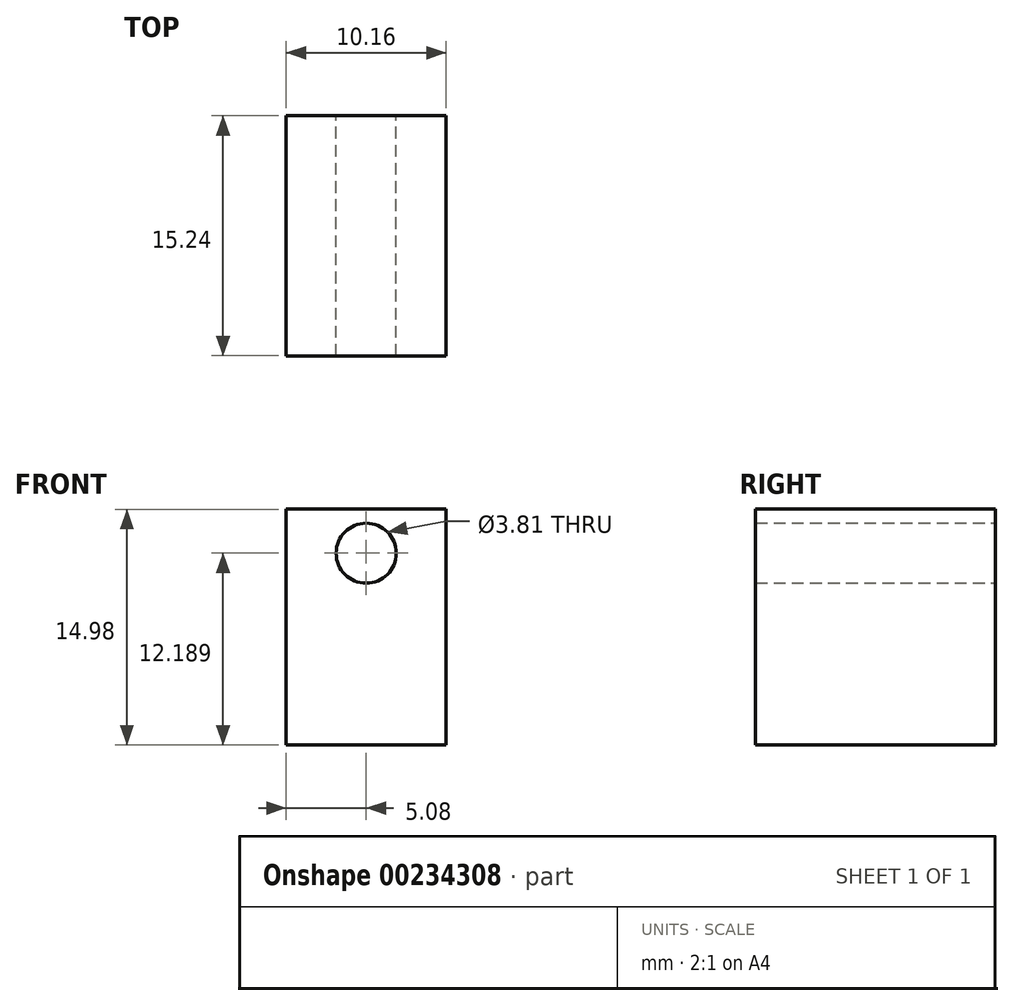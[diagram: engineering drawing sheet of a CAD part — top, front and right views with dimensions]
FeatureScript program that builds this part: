
annotation { "Feature Type Name" : "Feature", "Feature Type Description" : "" }
export const myFeature = defineFeature(function(context is Context, id is Id, definition is map)
    precondition{}
    {
        {
            var Q0;
            Q0=qCreatedBy(makeId("Front.planeOp"),FACE);
            var sketch = newSketch(context, id + "F0", { "sketchPlane" : qUnion([Q0])});
            skLineSegment(sketch, "E0.bottom", {"start": v(5.08, -7.5) * mm, "end": v(-5.08, -7.5) * mm});
            skLineSegment(sketch, "E0.top", {"start": v(5.08, 7.5) * mm, "end": v(-5.08, 7.5) * mm});
            skLineSegment(sketch, "E0.left", {"start": v(5.08, -7.5) * mm, "end": v(5.08, 7.5) * mm});
            skLineSegment(sketch, "E0.right", {"start": v(-5.08, -7.5) * mm, "end": v(-5.08, 7.5) * mm});
            skPoint(sketch, "E0.middle", {"position": v(0, 0) * mm});
            skCircle(sketch, "E1", {"center": v(0, 4.7) * mm, "radius": 1.9 * mm});
            skSolve(sketch);
        }
        {
            var Q0;
            Q0=makeQuery(id+"F0.imprint","IMPRINT",FACE,{"disambiguationData":[TD([[makeQuery(id+"F0.imprint","IMPRINT",EDGE,{"derivedFrom":sQuery(id+"F0.wireOp",EDGE,"E0.bottom")}),-1.0]])]});
            extrude(context, id + "F1", {"entities" : qUnion([Q0]), "depth" : 15.24 * mm, "offsetDistance" : 25 * mm});
        }
    });
